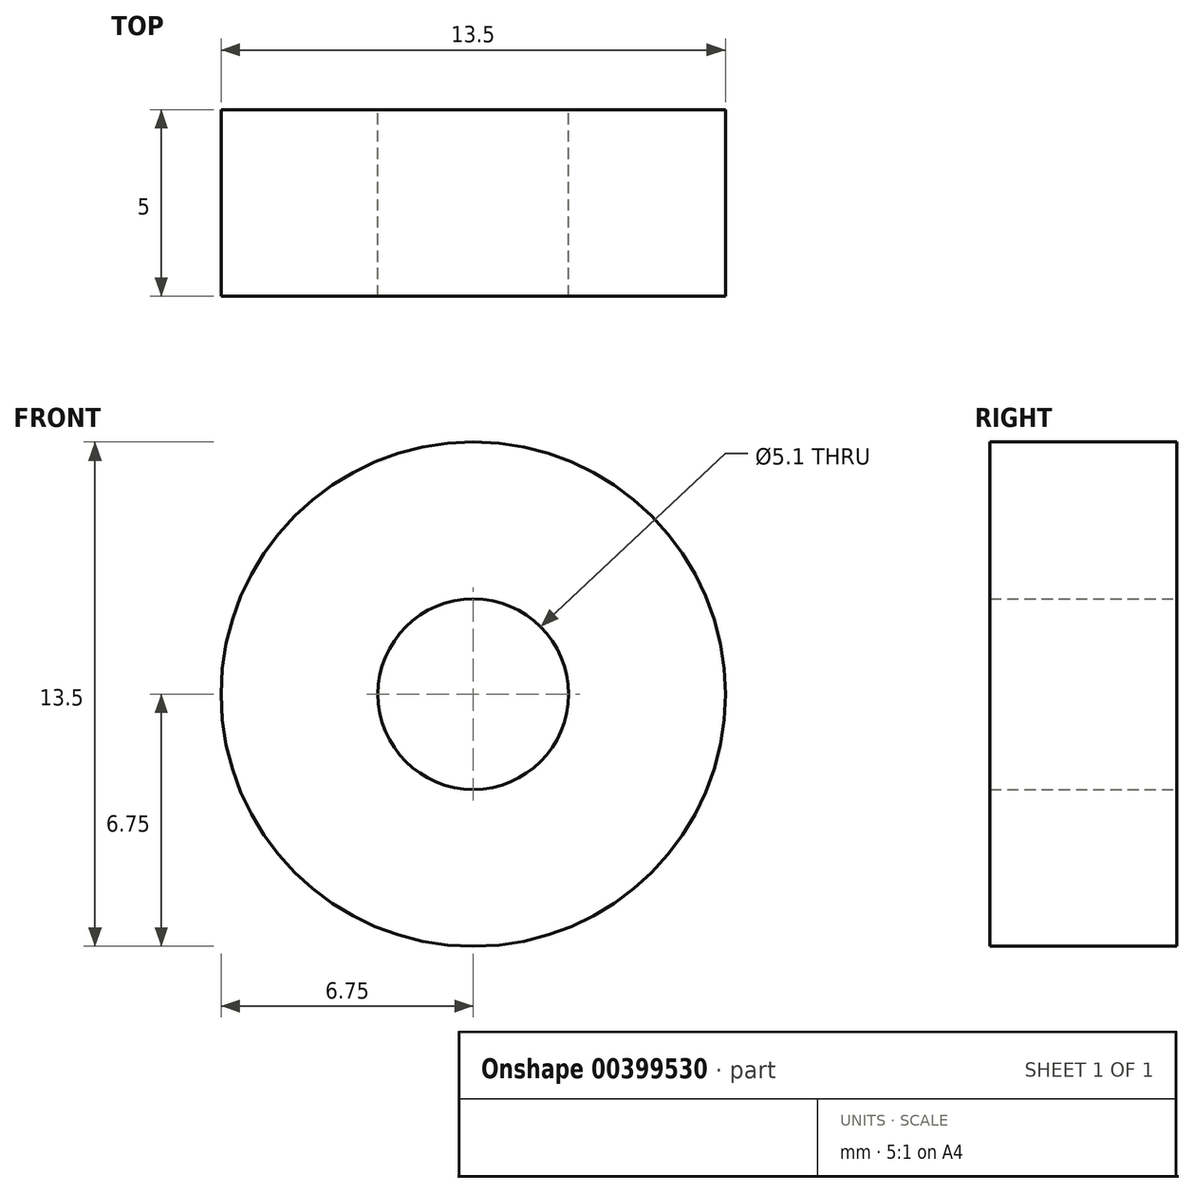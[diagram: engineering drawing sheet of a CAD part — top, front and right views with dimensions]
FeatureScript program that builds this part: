
annotation { "Feature Type Name" : "Feature", "Feature Type Description" : "" }
export const myFeature = defineFeature(function(context is Context, id is Id, definition is map)
    precondition{}
    {
        {
            var Q0;
            Q0=qCreatedBy(makeId("Front.planeOp"),FACE);
            var sketch = newSketch(context, id + "F0", { "sketchPlane" : qUnion([Q0])});
            skCircle(sketch, "E0", {"center": v(0, 0) * mm, "radius": 6.75 * mm});
            skCircle(sketch, "E1", {"center": v(0, 0) * mm, "radius": 2.55 * mm});
            skSolve(sketch);
        }
        {
            var Q0;
            Q0 = qSketchRegion(id + "F0", true);
            extrude(context, id + "F1", {"entities" : qUnion([Q0]), "depth" : 5 * mm});
        }
    });
